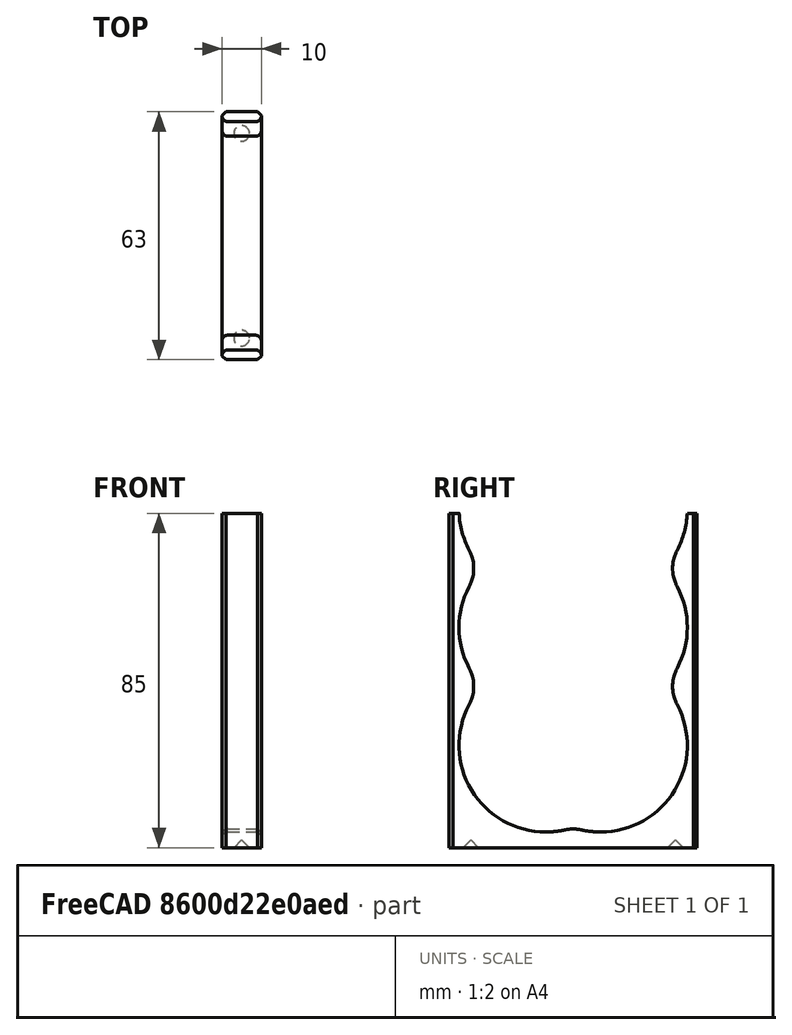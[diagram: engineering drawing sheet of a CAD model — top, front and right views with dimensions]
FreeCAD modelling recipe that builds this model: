
FCSTD DOCUMENT  (FreeCAD 0.16R6706 (Git))
Label: Dominion_Card_Tray_Rib
License: All rights reserved
LicenseURL: http://en.wikipedia.org/wiki/All_rights_reserved
objects: Part::Cylinder×6, Part::MultiFuse×2, Part::Cut×2, Part::Fillet×2, Part::Cone×2, Part::Box×1, Part::Chamfer×1
note: 16 computed .brp shape members not serialized (recipe doc carries the construction recipe); baked Part::Feature solids carry a one-line shape summary decoded from their .brp

FEATURE [Part::Box] Box036  label="Cube023"
  Height = 85
  Length = 10
  Placement = pos=(0,-31.5,0) rot=(0,0,1;0rad)
  Width = 63
FEATURE [Part::Cylinder] Cylinder029
  Angle = 360
  Height = 10
  Placement = pos=(0,7,26) rot=(0,1,0;1.5708rad)
  Radius = 22
FEATURE [Part::Cylinder] Cylinder026
  Angle = 360
  Height = 10
  Placement = pos=(0,-7,56) rot=(0,1,0;1.5708rad)
  Radius = 22
FEATURE [Part::Cylinder] Cylinder027
  Angle = 360
  Height = 10
  Placement = pos=(0,7,56) rot=(0,1,0;1.5708rad)
  Radius = 22
FEATURE [Part::Cylinder] Cylinder028
  Angle = 360
  Height = 10
  Placement = pos=(0,-7,26) rot=(0,1,0;1.5708rad)
  Radius = 22
FEATURE [Part::Cylinder] Cylinder030
  Angle = 360
  Height = 10
  Placement = pos=(0,-7,86) rot=(0,1,0;1.5708rad)
  Radius = 22
FEATURE [Part::Cylinder] Cylinder031
  Angle = 360
  Height = 10
  Placement = pos=(0,7,86) rot=(0,1,0;1.5708rad)
  Radius = 22
FEATURE [Part::MultiFuse] Fusion
  Shapes = -> [Cylinder029,Cylinder030,Cylinder031,Cylinder026,Cylinder027,Cylinder028]
FEATURE [Part::Cut] Cut
  Base = -> Box036
  Tool = -> Fusion
FEATURE [Part::Fillet] Fillet
  Base = -> Cut
  Edges = 5 edges r=10: [Edge18,Edge19,Edge24,Edge28,Edge30]
FEATURE [Part::Fillet] Fillet001
  Base = -> Fillet
  Edges = 2 edges r=1.5: [Edge13,Edge44]
FEATURE [Part::Chamfer] Chamfer
  Base = -> Fillet001
  Edges = 4 edges r=1: [Edge3,Edge7,Edge27,Edge34]
FEATURE [Part::Cone] Cone
  Angle = 360
  Height = 2
  Placement = pos=(5,-26,0) rot=(0,0,1;0rad)
  Radius1 = 2
  Radius2 = 0
FEATURE [Part::Cone] Cone001
  Angle = 360
  Height = 2
  Placement = pos=(5,26,0) rot=(0,0,1;0rad)
  Radius1 = 2
  Radius2 = 0
FEATURE [Part::MultiFuse] Fusion001
  Shapes = -> [Cone,Cone001]
FEATURE [Part::Cut] Cut001
  Base = -> Chamfer
  Tool = -> Fusion001
